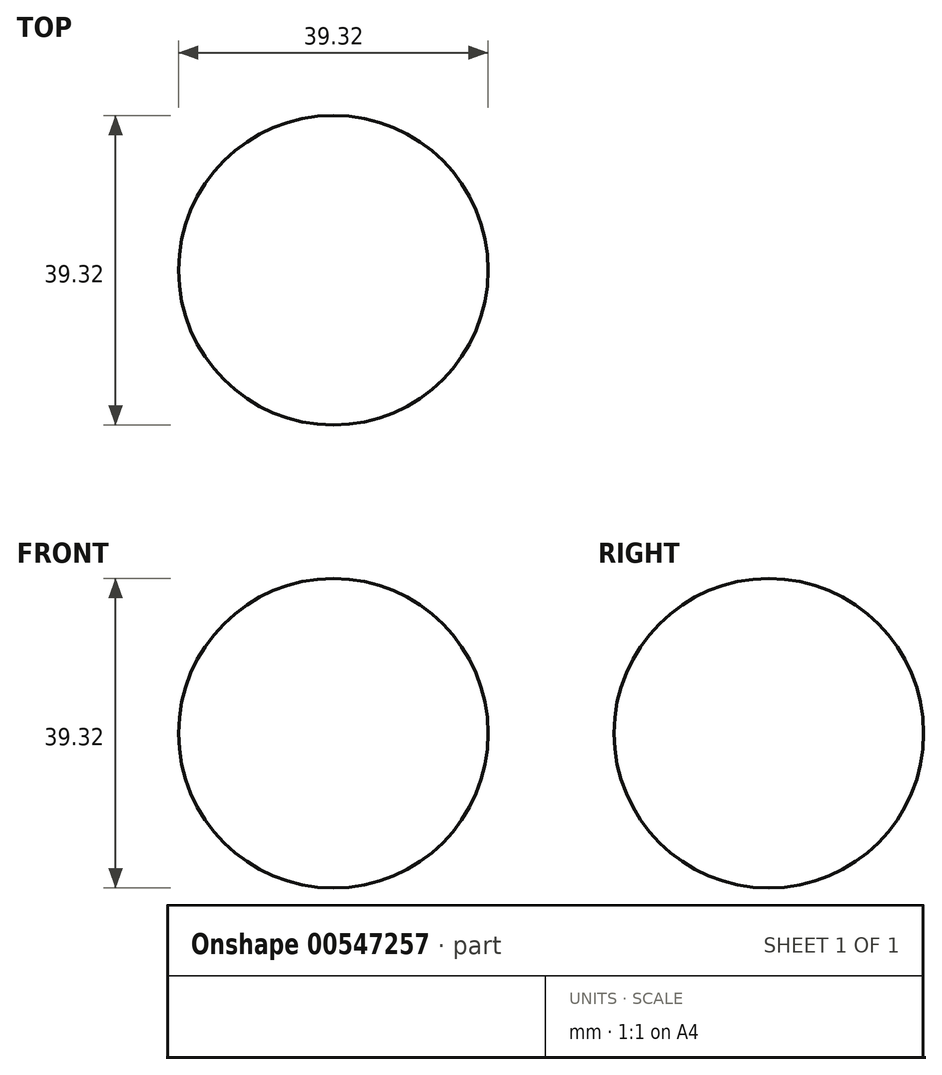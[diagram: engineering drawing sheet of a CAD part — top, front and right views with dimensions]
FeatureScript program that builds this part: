
annotation { "Feature Type Name" : "Feature", "Feature Type Description" : "" }
export const myFeature = defineFeature(function(context is Context, id is Id, definition is map)
    precondition{}
    {
        {
            var Q0;
            Q0=qCreatedBy(makeId("Front.planeOp"),FACE);
            var sketch = newSketch(context, id + "F0", { "sketchPlane" : qUnion([Q0])});
            skArc(sketch, "E0", {"start": v(0, -19.66) * mm, "mid": v(19.66, 0) * mm, "end": v(0, 19.66) * mm});
            skLineSegment(sketch, "E1", {"start": v(0, 19.66) * mm, "end": v(0, 0) * mm});
            skLineSegment(sketch, "E2", {"start": v(0, 0) * mm, "end": v(0, -19.66) * mm});
            skSolve(sketch);
        }
        {
            var Q0;
            Q0 = qSketchRegion(id + "F0", true);
            var Q1;
            Q1=sQuery(id+"F0.wireOp",EDGE,"E1");
            revolve(context, id + "F1", {"entities" : qUnion([Q0]), "axis" : qUnion([Q1]), "revolveType" : RevolveType.FULL});
        }
    });
